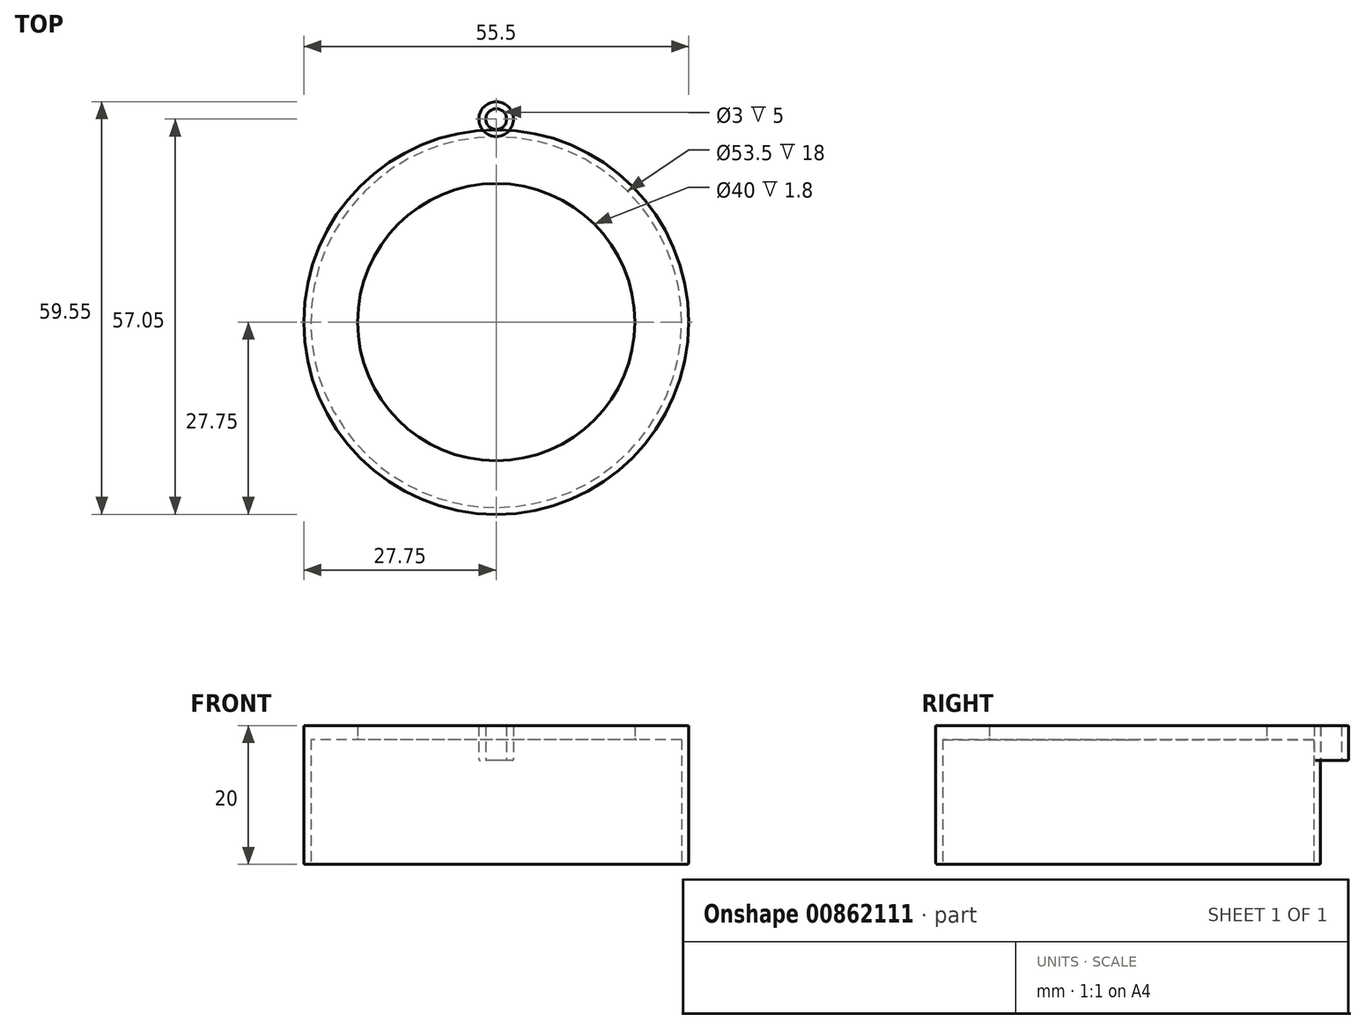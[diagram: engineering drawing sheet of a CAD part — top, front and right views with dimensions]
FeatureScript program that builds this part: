
annotation { "Feature Type Name" : "Feature", "Feature Type Description" : "" }
export const myFeature = defineFeature(function(context is Context, id is Id, definition is map)
    precondition{}
    {
        {
            var Q0;
            Q0=qCreatedBy(makeId("Top.planeOp"),FACE);
            var sketch = newSketch(context, id + "F0", { "sketchPlane" : qUnion([Q0])});
            skCircle(sketch, "E0", {"center": v(0, 0) * mm, "radius": 27.75 * mm});
            skSolve(sketch);
        }
        {
            var Q0;
            Q0 = qSketchRegion(id + "F0", true);
            extrude(context, id + "F1", {"entities" : qUnion([Q0]), "depth" : 20 * mm, "offsetDistance" : 25 * mm});
        }
        {
            var Q0;
            Q0=qCreatedBy(makeId("Top.planeOp"),FACE);
            var sketch = newSketch(context, id + "F2", { "sketchPlane" : qUnion([Q0])});
            skCircle(sketch, "E1", {"center": v(0, 0) * mm, "radius": 26.75 * mm});
            skSolve(sketch);
        }
        {
            var Q0;
            Q0 = qSketchRegion(id + "F2", true);
            extrude(context, id + "F3", {"entities" : qUnion([Q0]), "operationType" : NewBodyOperationType.REMOVE, "depth" : 18 * mm, "offsetDistance" : 25 * mm});
        }
        {
            var Q0;
            Q0=qCreatedBy(makeId("Top.planeOp"),FACE);
            var sketch = newSketch(context, id + "F4", { "sketchPlane" : qUnion([Q0])});
            skCircle(sketch, "E2", {"center": v(0, 0) * mm, "radius": 20 * mm});
            skSolve(sketch);
        }
        {
            var Q0;
            Q0 = qSketchRegion(id + "F4", true);
            extrude(context, id + "F5", {"entities" : qUnion([Q0]), "operationType" : NewBodyOperationType.REMOVE, "depth" : 20 * mm, "offsetDistance" : 25 * mm});
        }
        {
            var Q0;
            Q0=qCreatedBy(makeId("Top.planeOp"),FACE);
            var sketch = newSketch(context, id + "F6", { "sketchPlane" : qUnion([Q0])});
            skCircle(sketch, "E3", {"center": v(0, 0) * mm, "radius": 2.5 * mm});
            skSolve(sketch);
        }
        {
            var Q0;
            Q0 = qSketchRegion(id + "F6", true);
            extrude(context, id + "F7", {"entities" : qUnion([Q0]), "depth" : 5 * mm, "offsetDistance" : 25 * mm});
        }
        {
            var Q0;
            Q0=qCreatedBy(makeId("Top.planeOp"),FACE);
            var sketch = newSketch(context, id + "F8", { "sketchPlane" : qUnion([Q0])});
            skCircle(sketch, "E4", {"center": v(0, 0) * mm, "radius": 1.5 * mm});
            skSolve(sketch);
        }
        {
            var Q0;
            Q0 = qSketchRegion(id + "F8", true);
            extrude(context, id + "F9", {"entities" : qUnion([Q0]), "operationType" : NewBodyOperationType.REMOVE, "depth" : 5 * mm, "offsetDistance" : 25 * mm});
        }
        {
            var Q0;
            Q0=makeQuery(id+"F7.opExtrude","SWEPT_BODY",BODY,{"disambiguationData":[OSD([sQuery(id+"F6.wireOp",EDGE,"E3")])]});
            transform(context, id + "F10", {"entities" : qUnion([Q0]), "transformType" : TransformType.TRANSLATION_3D, "dx" : 0 * mm, "dy" : 29.1 * mm, "dz" : 15 * mm, "makeCopy" : false});
        }
        {
            var Q0;
            Q0=makeQuery(id+"F1.opExtrude","CAP_EDGE",EDGE,{"disambiguationData":[OSD([sQuery(id+"F0.wireOp",EDGE,"E0")])],"isStart":true});
            var Q1;
            Q1=makeQuery(id+"F3.boolean.opBoolean","COPY",EDGE,{"derivedFrom":makeQuery(id+"F3.opExtrude","CAP_EDGE",EDGE,{"disambiguationData":[OSD([sQuery(id+"F2.wireOp",EDGE,"E1")])],"isStart":true})});
            var Q2;
            Q2=makeQuery(id+"F5.boolean.opBoolean","INTERSECT",EDGE,{"derivedFrom":[makeQuery(id+"F3.boolean.opBoolean","COPY",FACE,{"derivedFrom":makeQuery(id+"F3.opExtrude","CAP_FACE",FACE,{"disambiguationData":[OSD([sQuery(id+"F2.wireOp",EDGE,"E1")])],"isStart":false})}),makeQuery(id+"F5.opExtrude","SWEPT_FACE",FACE,{"disambiguationData":[OSD([sQuery(id+"F4.wireOp",EDGE,"E2")])]})]});
            var Q3;
            Q3=makeQuery(id+"F9.boolean.opBoolean","COPY",EDGE,{"derivedFrom":makeQuery(id+"F9.opExtrude","CAP_EDGE",EDGE,{"disambiguationData":[OSD([sQuery(id+"F8.wireOp",EDGE,"E4")])],"isStart":true})});
            var Q4;
            Q4=makeQuery(id+"F7.opExtrude","CAP_EDGE",EDGE,{"disambiguationData":[OSD([sQuery(id+"F6.wireOp",EDGE,"E3")])],"isStart":true});
            fillet(context, id + "F11", {"entities" : qUnion([Q0, Q1, Q2, Q3, Q4]), "radius" : 0.2 * mm, "tangentPropagation" : true, "allowEdgeOverflow" : false});
        }
        {
            var Q0;
            Q0=makeQuery(id+"F7.opExtrude","SWEPT_BODY",BODY,{"disambiguationData":[OSD([sQuery(id+"F6.wireOp",EDGE,"E3")])]});
            transform(context, id + "F12", {"entities" : qUnion([Q0]), "transformType" : TransformType.TRANSLATION_3D, "dx" : 0 * mm, "dy" : 0.3 * mm, "dz" : 0 * mm, "makeCopy" : false});
        }
        {
            var Q0;
            Q0=makeQuery(id+"F7.opExtrude","SWEPT_BODY",BODY,{"disambiguationData":[OSD([sQuery(id+"F6.wireOp",EDGE,"E3")])]});
            transform(context, id + "F13", {"entities" : qUnion([Q0]), "transformType" : TransformType.TRANSLATION_3D, "dx" : 0 * mm, "dy" : -0.1 * mm, "dz" : 0 * mm, "makeCopy" : false});
        }
        {
            var Q0;
            Q0=makeQuery(id+"F7.opExtrude","SWEPT_BODY",BODY,{"disambiguationData":[OSD([sQuery(id+"F6.wireOp",EDGE,"E3")])]});
            transform(context, id + "F14", {"entities" : qUnion([Q0]), "transformType" : TransformType.TRANSLATION_3D, "dx" : 0 * mm, "dy" : 0 * mm, "dz" : 0 * mm, "makeCopy" : false});
        }
    });
